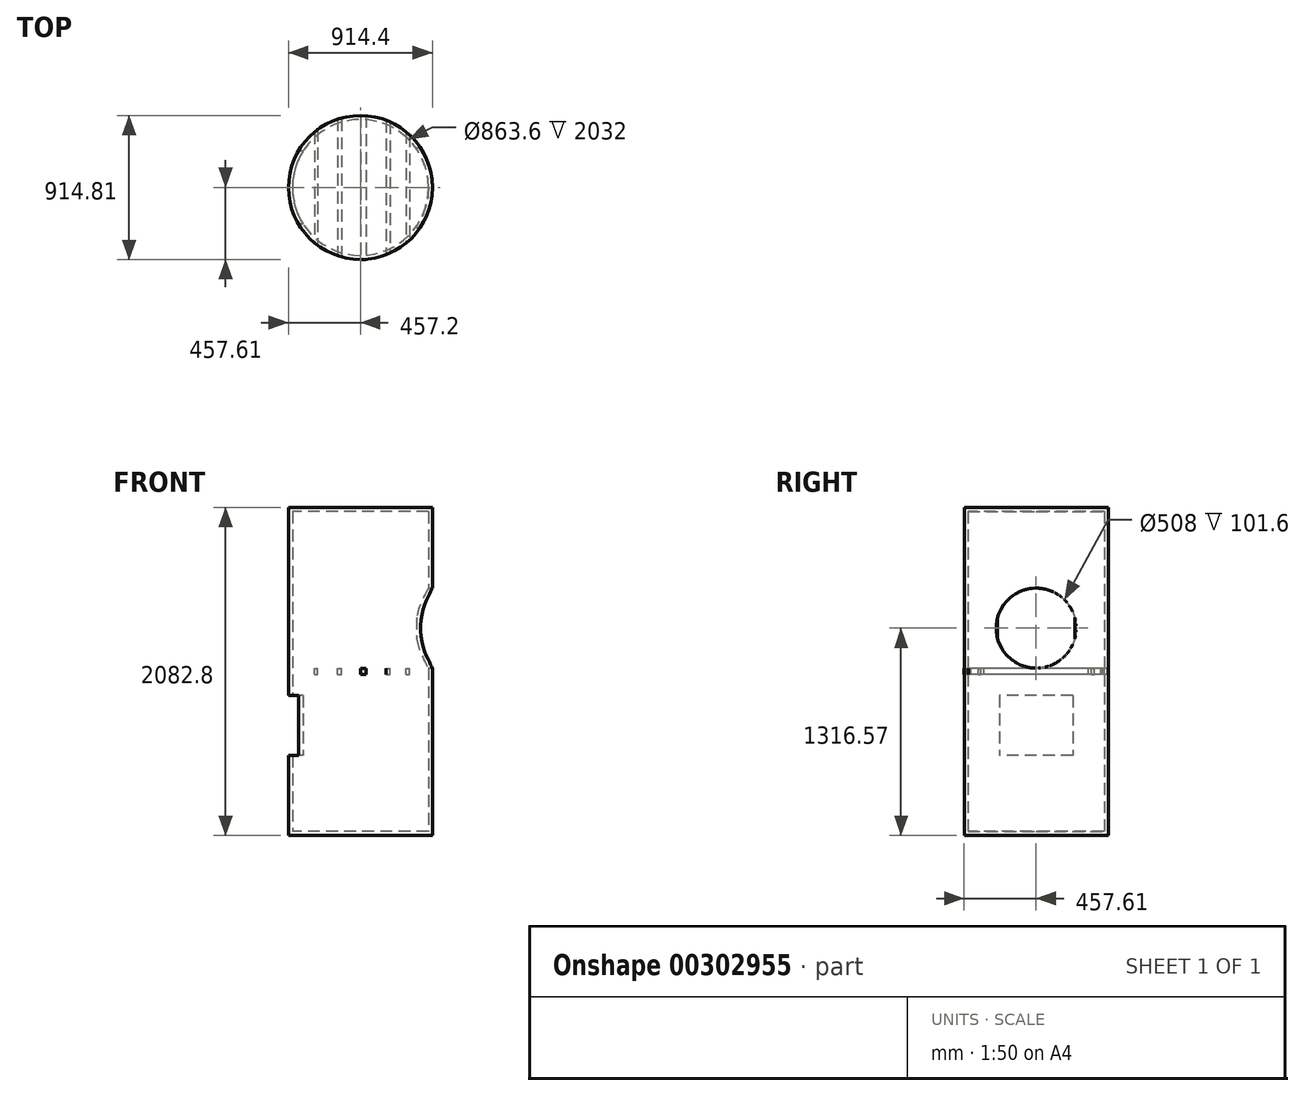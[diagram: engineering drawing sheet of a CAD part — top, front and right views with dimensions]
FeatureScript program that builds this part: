
annotation { "Feature Type Name" : "Feature", "Feature Type Description" : "" }
export const myFeature = defineFeature(function(context is Context, id is Id, definition is map)
    precondition{}
    {
        {
            var Q0;
            Q0=qCreatedBy(makeId("Top.planeOp"),FACE);
            var sketch = newSketch(context, id + "F0", { "sketchPlane" : qUnion([Q0])});
            skCircle(sketch, "E0", {"center": v(0, 0) * mm, "radius": 457.2 * mm});
            skPoint(sketch, "E1", {"position": v(457.2, 0) * mm});
            skPoint(sketch, "E2", {"position": v(-457.2, 0) * mm});
            skSolve(sketch);
        }
        {
            var Q0;
            Q0 = qSketchRegion(id + "F0", true);
            extrude(context, id + "F1", {"entities" : qUnion([Q0]), "depth" : 25.4 * mm});
        }
        {
            var Q0;
            Q0=makeQuery(id+"F1.opExtrude","CAP_FACE",FACE,{"disambiguationData":[OSD([sQuery(id+"F0.wireOp",EDGE,"E0")])],"isStart":false});
            var sketch = newSketch(context, id + "F2", { "sketchPlane" : qUnion([Q0])});
            skCircle(sketch, "E3", {"center": v(0, 0) * mm, "radius": 457.2 * mm});
            skCircle(sketch, "E4", {"center": v(0, 0) * mm, "radius": 431.8 * mm});
            skSolve(sketch);
        }
        {
            var Q0;
            Q0=makeQuery(id+"F2.imprint","IMPRINT",FACE,{"disambiguationData":[TD([[makeQuery(id+"F2.imprint","IMPRINT",EDGE,{"derivedFrom":sQuery(id+"F2.wireOp",EDGE,"E4")}),-1.0]])]});
            extrude(context, id + "F3", {"entities" : qUnion([Q0]), "operationType" : NewBodyOperationType.ADD, "depth" : 2032 * mm});
        }
        {
            var Q0;
            Q0=sQuery(id+"F0.wireOp",VERTEX,"E1");
            var Q1;
            Q1=qCreatedBy(makeId("Right.planeOp"),FACE);
            cPlane(context, id + "F4", {"entities" : qUnion([Q0, Q1]), "cplaneType" : CPlaneType.PLANE_POINT, "offset" : 25.4 * mm, "width" : 152.4 * mm, "height" : 152.4 * mm});
        }
        {
            var Q0;
            Q0=qCreatedBy(id+"F4.planeOp",FACE);
            var sketch = newSketch(context, id + "F5", { "sketchPlane" : qUnion([Q0])});
            skCircle(sketch, "E5", {"center": v(0, 1316.57) * mm, "radius": 254 * mm});
            skLineSegment(sketch, "E6", {"start": v(0, 1316.57) * mm, "end": v(0, 0) * mm, "construction": true});
            skSolve(sketch);
        }
        {
            var Q0;
            Q0=makeQuery(id+"F5.imprint","IMPRINT",FACE,{"disambiguationData":[TD([[makeQuery(id+"F5.imprint","IMPRINT",EDGE,{"derivedFrom":sQuery(id+"F5.wireOp",EDGE,"E5")}),1.0]])]});
            extrude(context, id + "F6", {"entities" : qUnion([Q0]), "operationType" : NewBodyOperationType.REMOVE, "oppositeDirection" : true, "depth" : 101.6 * mm});
        }
        {
            var Q0;
            Q0=sQuery(id+"F0.wireOp",VERTEX,"E2");
            var Q1;
            Q1=qCreatedBy(makeId("Right.planeOp"),FACE);
            cPlane(context, id + "F7", {"entities" : qUnion([Q0, Q1]), "cplaneType" : CPlaneType.PLANE_POINT, "offset" : 25.4 * mm, "width" : 152.4 * mm, "height" : 152.4 * mm});
        }
        {
            var Q0;
            Q0=qCreatedBy(id+"F7.planeOp",FACE);
            var sketch = newSketch(context, id + "F8", { "sketchPlane" : qUnion([Q0])});
            skLineSegment(sketch, "E7.bottom", {"start": v(-232.8, 508) * mm, "end": v(232.8, 508) * mm});
            skLineSegment(sketch, "E7.top", {"start": v(-232.8, 889) * mm, "end": v(232.8, 889) * mm});
            skLineSegment(sketch, "E7.left", {"start": v(-232.8, 508) * mm, "end": v(-232.8, 889) * mm});
            skLineSegment(sketch, "E7.right", {"start": v(232.8, 508) * mm, "end": v(232.8, 889) * mm});
            skLineSegment(sketch, "E8", {"start": v(0, 0) * mm, "end": v(0, 508) * mm, "construction": true});
            skLineSegment(sketch, "E9", {"start": v(232.8, 508) * mm, "end": v(0, 0) * mm, "construction": true});
            skLineSegment(sketch, "E10", {"start": v(-232.8, 508) * mm, "end": v(0, 0) * mm, "construction": true});
            skSolve(sketch);
        }
        {
            var Q0;
            Q0 = qSketchRegion(id + "F8", true);
            extrude(context, id + "F9", {"entities" : qUnion([Q0]), "operationType" : NewBodyOperationType.REMOVE, "depth" : 193.04 * mm});
        }
        {
            var Q0;
            Q0=makeQuery(id+"F3.opExtrude","CAP_FACE",FACE,{"disambiguationData":[OSD([sQuery(id+"F2.wireOp",EDGE,"E3"),sQuery(id+"F2.wireOp",EDGE,"E4")])],"isStart":false});
            var sketch = newSketch(context, id + "F10", { "sketchPlane" : qUnion([Q0])});
            skPoint(sketch, "E11", {"position": v(457.2, 0) * mm});
            skSolve(sketch);
        }
        {
            var Q0;
            Q0=makeQuery(id+"F10.imprint","IMPRINT",FACE,{"disambiguationData":[TD([[makeQuery(id+"F10.imprint","IMPRINT",EDGE,{"derivedFrom":makeQuery(id+"F3.opExtrude","CAP_EDGE",EDGE,{"disambiguationData":[OSD([sQuery(id+"F2.wireOp",EDGE,"E3")])],"isStart":false})}),1.0]])]});
            var sketch = newSketch(context, id + "F11", { "sketchPlane" : qUnion([Q0])});
            skCircle(sketch, "E12", {"center": v(0, 0) * mm, "radius": 457.2 * mm});
            skCircle(sketch, "E13", {"center": v(0, 0) * mm, "radius": 431.8 * mm});
            skSolve(sketch);
        }
        {
            var Q0;
            Q0 = qSketchRegion(id + "F11", true);
            var Q1;
            Q1=makeQuery(id+"F10.imprint","IMPRINT",FACE,{"disambiguationData":[TD([[makeQuery(id+"F10.imprint","IMPRINT",EDGE,{"derivedFrom":makeQuery(id+"F3.opExtrude","CAP_EDGE",EDGE,{"disambiguationData":[OSD([sQuery(id+"F2.wireOp",EDGE,"E3")])],"isStart":false})}),1.0]])]});
            var Q2;
            Q2=makeQuery(id+"F10.imprint","IMPRINT",FACE,{"disambiguationData":[TD([[makeQuery(id+"F10.imprint","IMPRINT",EDGE,{"derivedFrom":makeQuery(id+"F3.opExtrude","CAP_EDGE",EDGE,{"disambiguationData":[OSD([sQuery(id+"F2.wireOp",EDGE,"E4")])],"isStart":false})}),1.0]])]});
            extrude(context, id + "F12", {"entities" : qUnion([Q0, Q1, Q2]), "operationType" : NewBodyOperationType.ADD, "depth" : 25.4 * mm});
        }
        {
            var Q0;
            Q0=qCreatedBy(makeId("Right.planeOp"),FACE);
            var sketch = newSketch(context, id + "F13", { "sketchPlane" : qUnion([Q0])});
            skPoint(sketch, "E14", {"position": v(0, 1061.88) * mm});
            skLineSegment(sketch, "E15", {"start": v(0, 1061.88) * mm, "end": v(0, 0) * mm, "construction": true});
            skSolve(sketch);
        }
        {
            var Q0;
            Q0=sQuery(id+"F13.wireOp",VERTEX,"E14");
            var Q1;
            Q1=qCreatedBy(makeId("Top.planeOp"),FACE);
            cPlane(context, id + "F14", {"entities" : qUnion([Q0, Q1]), "cplaneType" : CPlaneType.PLANE_POINT, "offset" : 25.4 * mm, "width" : 152.4 * mm, "height" : 152.4 * mm});
        }
        {
            var Q0;
            Q0=qCreatedBy(id+"F14.planeOp",FACE);
            var sketch = newSketch(context, id + "F15", { "sketchPlane" : qUnion([Q0])});
            skLineSegment(sketch, "E16", {"start": v(0, 454.16) * mm, "end": v(0, -457.61) * mm});
            skLineSegment(sketch, "E17", {"start": v(-146.78, 433.44) * mm, "end": v(-146.78, -428.25) * mm});
            skLineSegment(sketch, "E18", {"start": v(162.32, 424.8) * mm, "end": v(162.32, -429.98) * mm});
            skLineSegment(sketch, "E19", {"start": v(-291.84, 350.55) * mm, "end": v(-291.84, -350.55) * mm});
            skLineSegment(sketch, "E20", {"start": v(290.1, 352.27) * mm, "end": v(290.1, -350.55) * mm});
            skLineSegment(sketch, "E21", {"start": v(0, 454.16) * mm, "end": v(37.13, 454.16) * mm});
            skLineSegment(sketch, "E22", {"start": v(37.13, 454.16) * mm, "end": v(37.13, -456.3) * mm});
            skLineSegment(sketch, "E23", {"start": v(37.13, -456.3) * mm, "end": v(0, -457.61) * mm});
            skLineSegment(sketch, "E24", {"start": v(-146.78, 433.44) * mm, "end": v(-120.08, 433.44) * mm});
            skLineSegment(sketch, "E25", {"start": v(-120.08, 433.44) * mm, "end": v(-120.08, -440.75) * mm});
            skLineSegment(sketch, "E26", {"start": v(-120.08, -440.75) * mm, "end": v(-146.78, -428.25) * mm});
            skLineSegment(sketch, "E27", {"start": v(-291.84, 350.55) * mm, "end": v(-272.1, 369.5) * mm});
            skLineSegment(sketch, "E28", {"start": v(-272.1, 369.5) * mm, "end": v(-272.1, -366.46) * mm});
            skLineSegment(sketch, "E29", {"start": v(-272.1, -366.46) * mm, "end": v(-291.84, -350.55) * mm});
            skLineSegment(sketch, "E30", {"start": v(162.32, 424.8) * mm, "end": v(187.44, 412.7) * mm});
            skLineSegment(sketch, "E31", {"start": v(187.44, 412.7) * mm, "end": v(187.44, -413.1) * mm});
            skLineSegment(sketch, "E32", {"start": v(187.44, -413.1) * mm, "end": v(162.32, -429.98) * mm});
            skLineSegment(sketch, "E33", {"start": v(290.1, 352.27) * mm, "end": v(311.82, 331.5) * mm});
            skLineSegment(sketch, "E34", {"start": v(311.82, 331.5) * mm, "end": v(311.82, -331.9) * mm});
            skLineSegment(sketch, "E35", {"start": v(311.82, -331.9) * mm, "end": v(290.1, -350.55) * mm});
            skSolve(sketch);
        }
        {
            var Q0;
            Q0=makeQuery(id+"F15.imprint","IMPRINT",FACE,{"disambiguationData":[TD([[makeQuery(id+"F15.imprint","IMPRINT",EDGE,{"derivedFrom":sQuery(id+"F15.wireOp",EDGE,"E19")}),1.0]])]});
            var Q1;
            Q1=makeQuery(id+"F15.imprint","IMPRINT",FACE,{"disambiguationData":[TD([[makeQuery(id+"F15.imprint","IMPRINT",EDGE,{"derivedFrom":sQuery(id+"F15.wireOp",EDGE,"E17")}),1.0]])]});
            var Q2;
            Q2=makeQuery(id+"F15.imprint","IMPRINT",FACE,{"disambiguationData":[TD([[makeQuery(id+"F15.imprint","IMPRINT",EDGE,{"derivedFrom":sQuery(id+"F15.wireOp",EDGE,"E16")}),1.0]])]});
            var Q3;
            Q3=makeQuery(id+"F15.imprint","IMPRINT",FACE,{"disambiguationData":[TD([[makeQuery(id+"F15.imprint","IMPRINT",EDGE,{"derivedFrom":sQuery(id+"F15.wireOp",EDGE,"E18")}),1.0]])]});
            var Q4;
            Q4=makeQuery(id+"F15.imprint","IMPRINT",FACE,{"disambiguationData":[TD([[makeQuery(id+"F15.imprint","IMPRINT",EDGE,{"derivedFrom":sQuery(id+"F15.wireOp",EDGE,"E20")}),1.0]])]});
            extrude(context, id + "F16", {"entities" : qUnion([Q0, Q1, Q2, Q3, Q4]), "oppositeDirection" : true, "depth" : 40.64 * mm});
        }
    });
